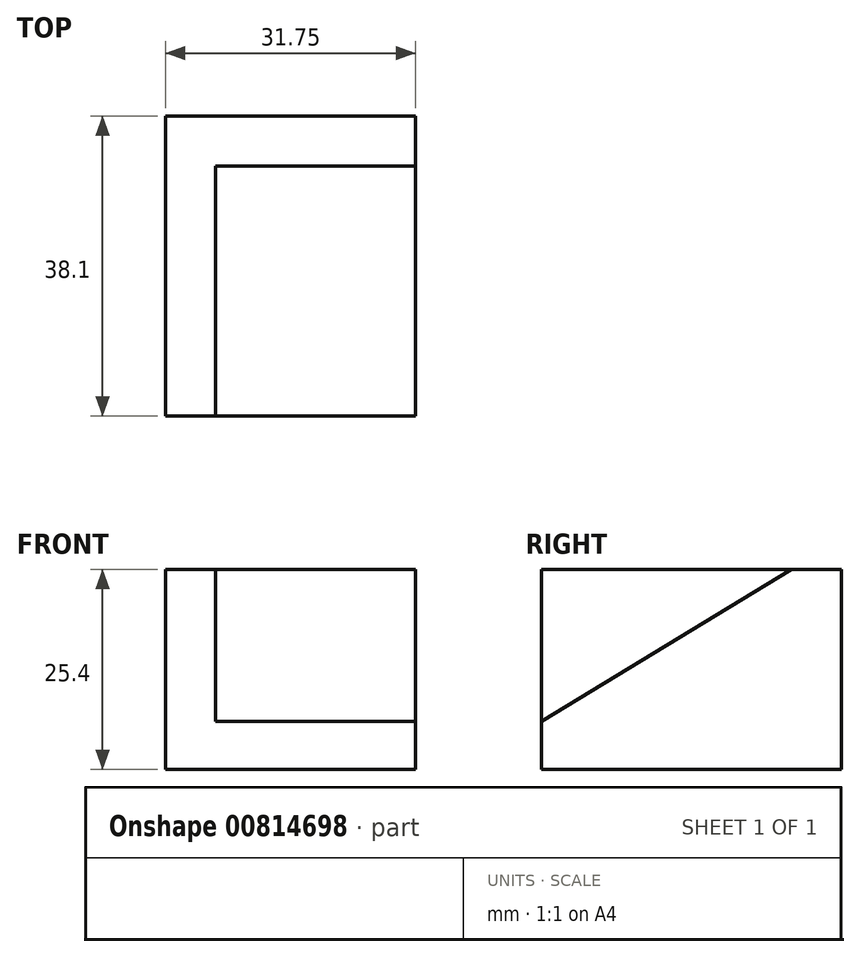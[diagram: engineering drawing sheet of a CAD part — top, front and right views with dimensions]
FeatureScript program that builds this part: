
annotation { "Feature Type Name" : "Feature", "Feature Type Description" : "" }
export const myFeature = defineFeature(function(context is Context, id is Id, definition is map)
    precondition{}
    {
        {
            var Q0;
            Q0=qCreatedBy(makeId("Right.planeOp"),FACE);
            var sketch = newSketch(context, id + "F0", { "sketchPlane" : qUnion([Q0])});
            skLineSegment(sketch, "E0", {"start": v(0, 0) * mm, "end": v(0, 25.4) * mm});
            skLineSegment(sketch, "E1", {"start": v(0, 25.4) * mm, "end": v(38.1, 25.4) * mm});
            skLineSegment(sketch, "E2", {"start": v(38.1, 25.4) * mm, "end": v(38.1, 0) * mm});
            skLineSegment(sketch, "E3", {"start": v(38.1, 0) * mm, "end": v(0, 0) * mm});
            skSolve(sketch);
        }
        {
            var Q0;
            Q0 = qSketchRegion(id + "F0", true);
            extrude(context, id + "F1", {"entities" : qUnion([Q0]), "depth" : 31.75 * mm, "offsetDistance" : 25.4 * mm});
        }
        {
            var Q0;
            Q0=makeQuery(id+"F1.opExtrude","CAP_FACE",FACE,{"disambiguationData":[OSD([sQuery(id+"F0.wireOp",EDGE,"E0"),sQuery(id+"F0.wireOp",EDGE,"E1"),sQuery(id+"F0.wireOp",EDGE,"E2"),sQuery(id+"F0.wireOp",EDGE,"E3")])],"isStart":false});
            var sketch = newSketch(context, id + "F2", { "sketchPlane" : qUnion([Q0])});
            skLineSegment(sketch, "E4", {"start": v(0, 0) * mm, "end": v(0, 6.13) * mm});
            skLineSegment(sketch, "E5", {"start": v(38.1, 25.4) * mm, "end": v(31.75, 25.4) * mm});
            skLineSegment(sketch, "E6", {"start": v(31.75, 25.4) * mm, "end": v(0, 6.13) * mm});
            skSolve(sketch);
        }
        {
            var Q0;
            Q0 = qSketchRegion(id + "F2", true);
            var Q1;
            {var subQ0=sQuery(id+"F2.wireOp",EDGE,"E6");Q1=makeQuery(id+"F2.imprint","IMPRINT",FACE,{"disambiguationData":[TD([[makeQuery(id+"F2.imprint","IMPRINT",EDGE,{"derivedFrom":subQ0}),-1.0]])]});}
            extrude(context, id + "F3", {"entities" : qUnion([Q0, Q1]), "operationType" : NewBodyOperationType.REMOVE, "oppositeDirection" : true, "depth" : 25.4 * mm, "offsetDistance" : 25.4 * mm});
        }
    });
